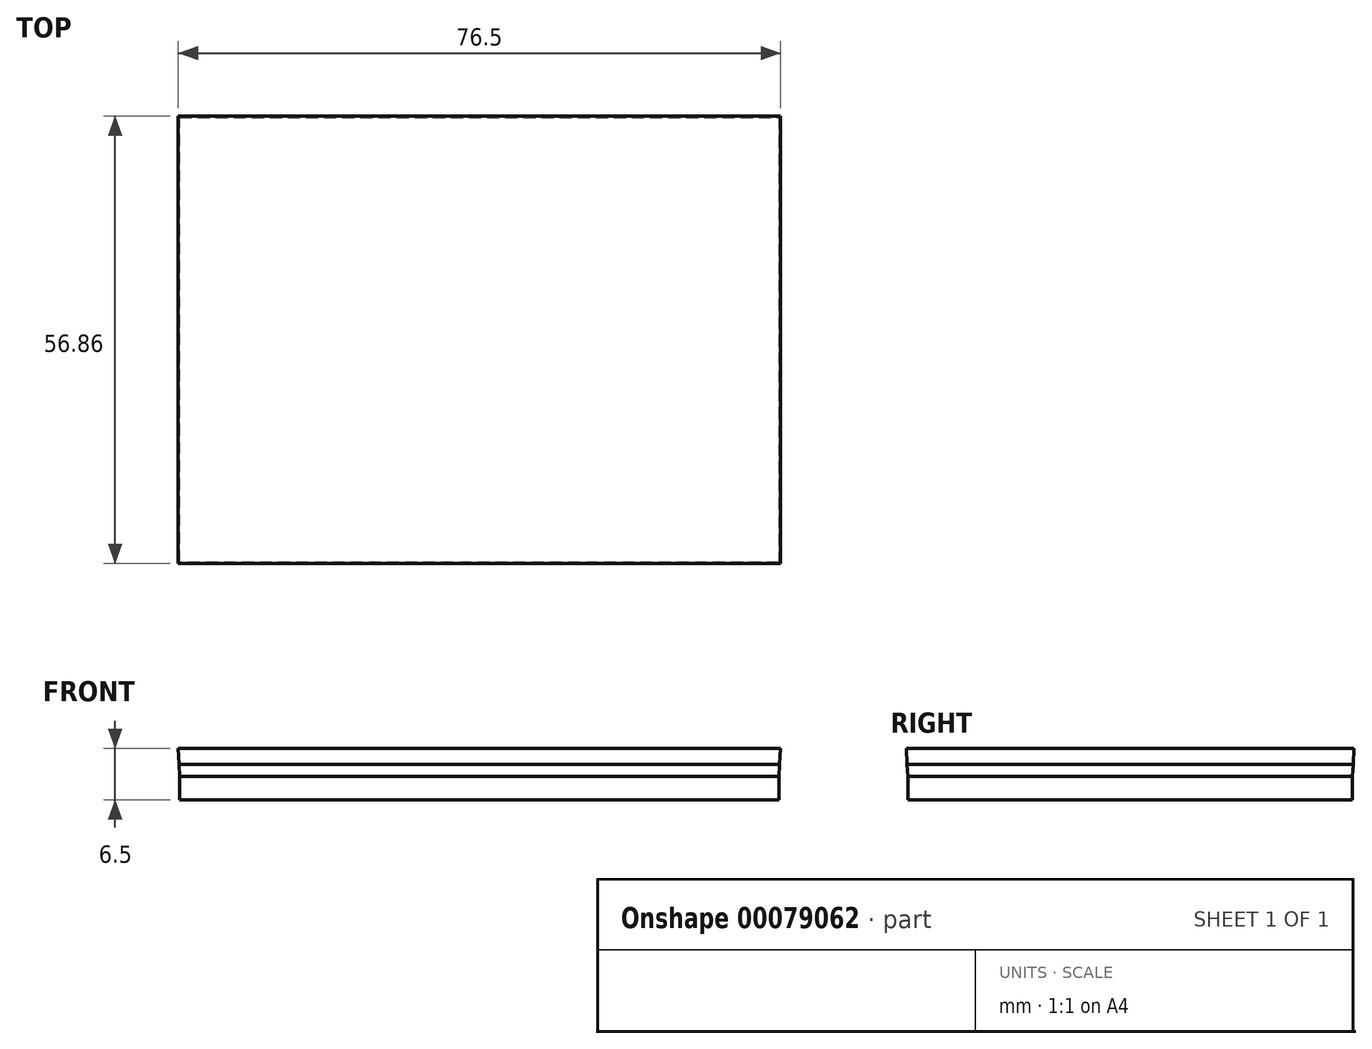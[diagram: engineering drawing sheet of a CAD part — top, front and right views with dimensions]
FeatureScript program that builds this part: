
annotation { "Feature Type Name" : "Feature", "Feature Type Description" : "" }
export const myFeature = defineFeature(function(context is Context, id is Id, definition is map)
    precondition{}
    {
        {
            var Q0;
            Q0=qCreatedBy(makeId("Top.planeOp"),FACE);
            var sketch = newSketch(context, id + "F0", { "sketchPlane" : qUnion([Q0])});
            skLineSegment(sketch, "E0.bottom", {"start": v(-76.14, 56.5) * mm, "end": v(0, 56.5) * mm});
            skLineSegment(sketch, "E0.top", {"start": v(-76.14, 0) * mm, "end": v(0, 0) * mm});
            skLineSegment(sketch, "E0.left", {"start": v(-76.14, 56.5) * mm, "end": v(-76.14, 0) * mm});
            skLineSegment(sketch, "E0.right", {"start": v(0, 56.5) * mm, "end": v(0, 0) * mm});
            skSolve(sketch);
        }
        {
            var Q0;
            Q0=qSketchRegion(id+"F0",true);
            extrude(context, id + "F1", {"entities" : qUnion([Q0]), "depth" : 3 * mm});
        }
        {
            var Q0;
            Q0=makeQuery(id+"F1.opExtrude","CAP_FACE",FACE,{"disambiguationData":[OSD([sQuery(id+"F0.wireOp",EDGE,"E0.bottom"),sQuery(id+"F0.wireOp",EDGE,"E0.top"),sQuery(id+"F0.wireOp",EDGE,"E0.left"),sQuery(id+"F0.wireOp",EDGE,"E0.right")])],"isStart":false});
            var sketch = newSketch(context, id + "F2", { "sketchPlane" : qUnion([Q0])});
            skLineSegment(sketch, "E1.bottom", {"start": v(-76.14, 56.5) * mm, "end": v(0, 56.5) * mm});
            skLineSegment(sketch, "E1.top", {"start": v(-76.14, 0) * mm, "end": v(0, 0) * mm});
            skLineSegment(sketch, "E1.left", {"start": v(-76.14, 56.5) * mm, "end": v(-76.14, 0) * mm});
            skLineSegment(sketch, "E1.right", {"start": v(0, 56.5) * mm, "end": v(0, 0) * mm});
            skSolve(sketch);
        }
        {
            var Q0;
            Q0=makeQuery(id+"F2.imprint","IMPRINT",FACE,{"disambiguationData":[TD([[makeQuery(id+"F2.imprint","IMPRINT",EDGE,{"derivedFrom":sQuery(id+"F2.wireOp",EDGE,"E1.bottom")}),-1.0]])]});
            extrude(context, id + "F3", {"entities" : qUnion([Q0]), "depth" : 1.5 * mm, "hasDraft" : true, "draftAngle" : 3 * degree});
        }
        {
            var Q0;
            Q0=makeQuery(id+"F3.opExtrude","CAP_FACE",FACE,{"disambiguationData":[OSD([sQuery(id+"F2.wireOp",EDGE,"E1.bottom"),sQuery(id+"F2.wireOp",EDGE,"E1.top"),sQuery(id+"F2.wireOp",EDGE,"E1.left"),sQuery(id+"F2.wireOp",EDGE,"E1.right")])],"isStart":false});
            var sketch = newSketch(context, id + "F4", { "sketchPlane" : qUnion([Q0])});
            skLineSegment(sketch, "E2.bottom", {"start": v(-76.22, 56.58) * mm, "end": v(0.08, 56.58) * mm});
            skLineSegment(sketch, "E2.top", {"start": v(-76.22, -0.08) * mm, "end": v(0.08, -0.08) * mm});
            skLineSegment(sketch, "E2.left", {"start": v(-76.22, 56.58) * mm, "end": v(-76.22, -0.08) * mm});
            skLineSegment(sketch, "E2.right", {"start": v(0.08, 56.58) * mm, "end": v(0.08, -0.08) * mm});
            skSolve(sketch);
        }
        {
            var Q0;
            Q0 = qSketchRegion(id + "F4", true);
            extrude(context, id + "F5", {"entities" : qUnion([Q0]), "depth" : 2 * mm, "hasDraft" : true, "draftAngle" : 3 * degree});
        }
    });
